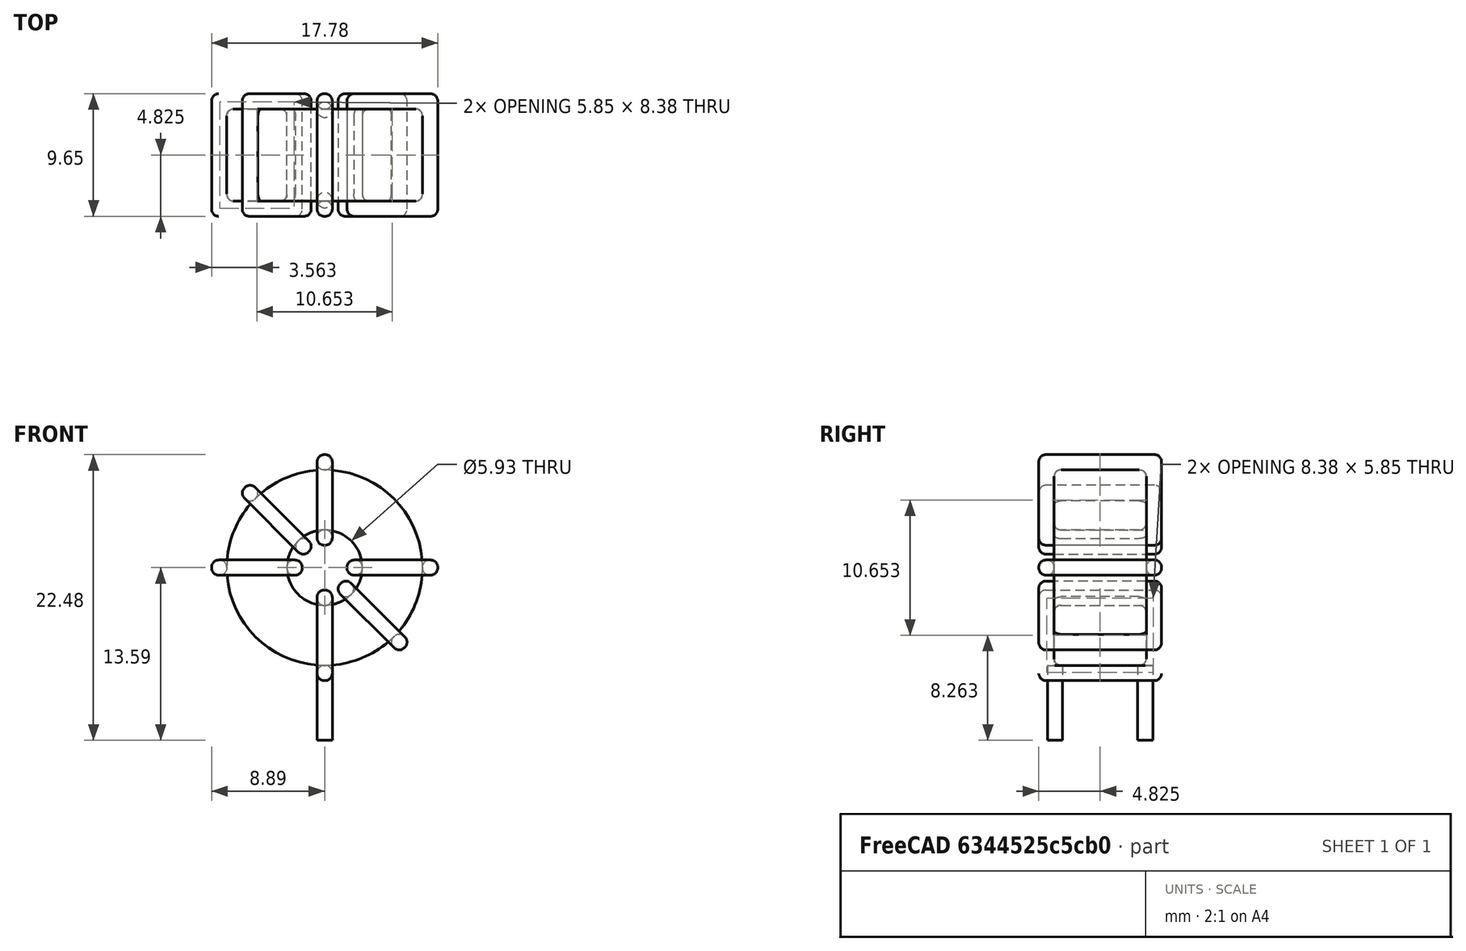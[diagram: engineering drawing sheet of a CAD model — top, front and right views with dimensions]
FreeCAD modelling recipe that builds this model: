
FCSTD DOCUMENT  (FreeCAD 0.16R6703 (Git))
Label: L_Toroid_Vertical_L17.8mm_W9.7mm_P7.11mm_Pulse_B
License: All rights reserved
LicenseURL: http://en.wikipedia.org/wiki/All_rights_reserved
objects: Sketcher::SketchObject×6, PartDesign::Pad×6, PartDesign::Fillet×5, Spreadsheet::Sheet×1
note: 23 computed .brp shape members not serialized (recipe doc carries the construction recipe); baked Part::Feature solids carry a one-line shape summary decoded from their .brp

FEATURE [Spreadsheet::Sheet] Spreadsheet  label="dimensions"
  cells = A1=Wx; B1(Wx)=17.78; C1(WW)=5.926666666666667; D1=17.78; A2=Wy; B2(Wy)=9.65; D2=9.65; A3=RM; B3(RMx)=7.11; C3(RMy)=0; A4=d_wire; B4(d_wire)=1.2; A5=H; B5(H)=17.78; A6=offsetx; B6(offsetx)=8.890000000000001
FEATURE [Sketcher::SketchObject] Sketch
  Placement = pos=(0,-3.555,0) rot=(1,0,0;1.5708rad)
  expr: Placement.Base.y = -Spreadsheet.RMx / 2
  expr: Constraints[0] = Spreadsheet.Wx / 2 - Spreadsheet.d_wire
  expr: Constraints[4] = Spreadsheet.WW / 2
  expr: Constraints[2] = Spreadsheet.Wx / 2 + Spreadsheet.d_wire + 0.5
  sketch-geometry (2):
    g0: Circle CenterX=0 CenterY=10.59 CenterZ=0 NormalX=0 NormalY=0 NormalZ=1 Radius=7.69
    g1: Circle CenterX=0 CenterY=10.59 CenterZ=0 NormalX=0 NormalY=0 NormalZ=1 Radius=2.96333
  constraints (5):
    c: Radius(g0) = 7.69
    c: DistanceX(g-1,g0) = 0
    c: DistanceY(g-1,g0) = 10.59
    c: Coincident(g1,g0)
    c: Radius(g1) = 2.96333
FEATURE [PartDesign::Pad] Pad
  Length = 7.25
  Length2 = 100
  Midplane = true
  Placement = pos=(0,-3.555,0) rot=(1,0,0;1.5708rad)
  Sketch = -> Sketch
  Type = 0
  expr: Length = Spreadsheet.Wy - 2 * Spreadsheet.d_wire
FEATURE [Sketcher::SketchObject] Sketch001
  Placement = pos=(0,0,1.7) rot=(0,0,1;0rad)
  expr: Placement.Base.z = 0.5 + Spreadsheet.d_wire
  expr: Constraints[4] = Spreadsheet.RMy
  expr: Constraints[2] = -Spreadsheet.RMx
  expr: Constraints[1] = Spreadsheet.d_wire / 2
  sketch-geometry (2):
    g0: Circle CenterX=0 CenterY=0 CenterZ=0 NormalX=0 NormalY=0 NormalZ=1 Radius=0.6
    g1: Circle CenterX=0 CenterY=-7.11 CenterZ=0 NormalX=0 NormalY=0 NormalZ=1 Radius=0.6
  constraints (5):
    c: Equal(g0,g1)
    c: Radius(g0) = 0.6
    c: DistanceY(g-1,g1) = -7.11
    c: Coincident(g0,g-1)
    c: DistanceX(g-1,g1) = 0
FEATURE [PartDesign::Pad] Pad001
  Length = 1.2
  Length2 = 4.7
  Placement = pos=(0,0,1.7) rot=(0,0,1;0rad)
  Reversed = true
  Sketch = -> Sketch001
  Type = 4
  expr: Length2 = 3.5 + Spreadsheet.d_wire
  expr: Length = Spreadsheet.d_wire
FEATURE [PartDesign::Fillet] Fillet
  Base = -> Pad [Edge6,Edge3,Edge2]
  Placement = pos=(0,-3.555,0) rot=(1,0,0;1.5708rad)
  Radius = 0.5
FEATURE [Sketcher::SketchObject] Sketch003
  Placement = pos=(0,1.27,10.59) rot=(1,0,0;3.14159rad)
  expr: Constraints[18] = Spreadsheet.d_wire
  expr: Constraints[16] = Spreadsheet.d_wire
  expr: Constraints[19] = Spreadsheet.d_wire
  expr: Constraints[17] = Spreadsheet.d_wire
  expr: Placement.Base.y = -1 * (Spreadsheet.RMx - Spreadsheet.Wy) / 2
  expr: Constraints[21] = (Spreadsheet.Wx - Spreadsheet.WW) / 2 - Spreadsheet.d_wire
  expr: Constraints[22] = Spreadsheet.Wx / 2 - Spreadsheet.d_wire
  expr: Constraints[43] = Spreadsheet.d_wire
  expr: Constraints[48] = Spreadsheet.Wx - Spreadsheet.d_wire * 2
  expr: Constraints[49] = Spreadsheet.Wy
  expr: Placement.Base.z = Spreadsheet.Wx / 2 + Spreadsheet.d_wire + 0.5
  sketch-geometry (16):
    g0: LineSegment StartX=-1.76333 StartY=0 StartZ=0 EndX=-8.89 EndY=0 EndZ=0
    g1: LineSegment StartX=-8.89 StartY=0 StartZ=0 EndX=-8.89 EndY=9.65 EndZ=0
    g2: LineSegment StartX=-8.89 StartY=9.65 StartZ=0 EndX=-1.76333 EndY=9.65 EndZ=0
    g3: LineSegment StartX=-1.76333 StartY=9.65 StartZ=0 EndX=-1.76333 EndY=0 EndZ=0
    g4: LineSegment StartX=-7.69 StartY=8.45 StartZ=0 EndX=-2.96333 EndY=8.45 EndZ=0
    g5: LineSegment StartX=-2.96333 StartY=8.45 StartZ=0 EndX=-2.96333 EndY=1.2 EndZ=0
    g6: LineSegment StartX=-2.96333 StartY=1.2 StartZ=0 EndX=-7.69 EndY=1.2 EndZ=0
    g7: LineSegment StartX=-7.69 StartY=1.2 StartZ=0 EndX=-7.69 EndY=8.45 EndZ=0
    g8: LineSegment StartX=1.76333 StartY=9.65 StartZ=0 EndX=8.89 EndY=9.65 EndZ=0
    g9: LineSegment StartX=8.89 StartY=9.65 StartZ=0 EndX=8.89 EndY=0 EndZ=0
    g10: LineSegment StartX=8.89 StartY=0 StartZ=0 EndX=1.76333 EndY=0 EndZ=0
    g11: LineSegment StartX=1.76333 StartY=0 StartZ=0 EndX=1.76333 EndY=9.65 EndZ=0
    g12: LineSegment StartX=2.96333 StartY=8.45 StartZ=0 EndX=7.69 EndY=8.45 EndZ=0
    g13: LineSegment StartX=7.69 StartY=8.45 StartZ=0 EndX=7.69 EndY=1.2 EndZ=0
    g14: LineSegment StartX=7.69 StartY=1.2 StartZ=0 EndX=2.96333 EndY=1.2 EndZ=0
    g15: LineSegment StartX=2.96333 StartY=1.2 StartZ=0 EndX=2.96333 EndY=8.45 EndZ=0
  constraints (50):
    c: Horizontal(g0)
    c: Coincident(g1,g0)
    c: Vertical(g1)
    c: Coincident(g2,g1)
    c: Horizontal(g2)
    c: Coincident(g3,g2)
    c: Coincident(g3,g0)
    c: Vertical(g3)
    c: Coincident(g4,g5)
    c: Coincident(g5,g6)
    c: Coincident(g6,g7)
    c: Coincident(g7,g4)
    c: Horizontal(g4)
    c: Horizontal(g6)
    c: Vertical(g5)
    c: Vertical(g7)
    c: DistanceX(g1,g4) = 1.2
    c: DistanceY(g4,g1) = 1.2
    c: DistanceX(g5,g0) = 1.2
    c: DistanceY(g0,g5) = 1.2
    c: DistanceY(g-1,g0) = 0
    c: DistanceX(g6,g6) = 4.72667
    c: DistanceX(g6,g-1) = 7.69
    c: Coincident(g8,g9)
    c: Coincident(g9,g10)
    c: Coincident(g10,g11)
    c: Coincident(g11,g8)
    c: Horizontal(g8)
    c: Horizontal(g10)
    c: Vertical(g9)
    c: Vertical(g11)
    c: Coincident(g12,g13)
    c: Coincident(g13,g14)
    c: Coincident(g14,g15)
    c: Coincident(g15,g12)
    c: Horizontal(g12)
    c: Horizontal(g14)
    c: Vertical(g13)
    c: Vertical(g15)
    c: DistanceY(g8,g2) = 0
    c: DistanceY(g10,g0) = 0
    c: DistanceY(g14,g5) = 0
    c: DistanceY(g12,g4) = 0
    c: DistanceX(g8,g12) = 1.2
    c: Equal(g8,g2)
    c: Equal(g12,g4)
    c: Equal(g9,g1)
    c: Equal(g13,g7)
    c: DistanceX(g4,g12) = 15.38
    c: DistanceY(g0,g1) = 9.65
FEATURE [PartDesign::Pad] Pad002
  Length = 1.2
  Length2 = 100
  Midplane = true
  Placement = pos=(0,1.27,10.59) rot=(1,0,0;3.14159rad)
  Sketch = -> Sketch003
  Type = 0
  expr: Length = Spreadsheet.d_wire
FEATURE [PartDesign::Fillet] Fillet001
  Base = -> Pad002 [Edge38,Edge41,Edge42,Edge43,Edge29,Edge32,Edge33,Edge34,Edge25,Edge35,Edge36,Edge13,Edge14,Edge15,Edge16,Edge17,Edge18,Edge19,Edge1,Edge2,Edge3,Edge4,Edge5,Edge6,Edge7,Edge37,Edge39,Edge40,Edge20,Edge23,Edge24,Edge21,Edge22,Edge8,Edge9,Edge10,Edge11,Edge12,Edge26,Edge27,+8 more]
  Placement = pos=(0,1.27,10.59) rot=(1,0,0;3.14159rad)
  Radius = 0.564
  expr: Radius = Spreadsheet.d_wire * 0.47
FEATURE [Sketcher::SketchObject] Sketch004
  Placement = pos=(0,1.27,10.59) rot=(0.92388,0,0.382683;3.14159rad)
  expr: Constraints[18] = Spreadsheet.d_wire
  expr: Constraints[16] = Spreadsheet.d_wire
  expr: Constraints[19] = Spreadsheet.d_wire
  expr: Constraints[17] = Spreadsheet.d_wire
  expr: Placement.Base.y = -1 * (Spreadsheet.RMx - Spreadsheet.Wy) / 2
  expr: Constraints[21] = (Spreadsheet.Wx - Spreadsheet.WW) / 2 - Spreadsheet.d_wire
  expr: Constraints[22] = Spreadsheet.Wx / 2 - Spreadsheet.d_wire
  expr: Constraints[43] = Spreadsheet.d_wire
  expr: Constraints[48] = Spreadsheet.Wx - 2 * Spreadsheet.d_wire
  expr: Constraints[49] = Spreadsheet.Wy
  expr: Placement.Base.z = Spreadsheet.Wx / 2 + Spreadsheet.d_wire + 0.5
  sketch-geometry (16):
    g0: LineSegment StartX=-1.76333 StartY=0 StartZ=0 EndX=-8.89 EndY=0 EndZ=0
    g1: LineSegment StartX=-8.89 StartY=0 StartZ=0 EndX=-8.89 EndY=9.65 EndZ=0
    g2: LineSegment StartX=-8.89 StartY=9.65 StartZ=0 EndX=-1.76333 EndY=9.65 EndZ=0
    g3: LineSegment StartX=-1.76333 StartY=9.65 StartZ=0 EndX=-1.76333 EndY=0 EndZ=0
    g4: LineSegment StartX=-7.69 StartY=8.45 StartZ=0 EndX=-2.96333 EndY=8.45 EndZ=0
    g5: LineSegment StartX=-2.96333 StartY=8.45 StartZ=0 EndX=-2.96333 EndY=1.2 EndZ=0
    g6: LineSegment StartX=-2.96333 StartY=1.2 StartZ=0 EndX=-7.69 EndY=1.2 EndZ=0
    g7: LineSegment StartX=-7.69 StartY=1.2 StartZ=0 EndX=-7.69 EndY=8.45 EndZ=0
    g8: LineSegment StartX=1.76333 StartY=9.65 StartZ=0 EndX=8.89 EndY=9.65 EndZ=0
    g9: LineSegment StartX=8.89 StartY=9.65 StartZ=0 EndX=8.89 EndY=0 EndZ=0
    g10: LineSegment StartX=8.89 StartY=0 StartZ=0 EndX=1.76333 EndY=0 EndZ=0
    g11: LineSegment StartX=1.76333 StartY=0 StartZ=0 EndX=1.76333 EndY=9.65 EndZ=0
    g12: LineSegment StartX=2.96333 StartY=8.45 StartZ=0 EndX=7.69 EndY=8.45 EndZ=0
    g13: LineSegment StartX=7.69 StartY=8.45 StartZ=0 EndX=7.69 EndY=1.2 EndZ=0
    g14: LineSegment StartX=7.69 StartY=1.2 StartZ=0 EndX=2.96333 EndY=1.2 EndZ=0
    g15: LineSegment StartX=2.96333 StartY=1.2 StartZ=0 EndX=2.96333 EndY=8.45 EndZ=0
  constraints (50):
    c: Horizontal(g0)
    c: Coincident(g1,g0)
    c: Vertical(g1)
    c: Coincident(g2,g1)
    c: Horizontal(g2)
    c: Coincident(g3,g2)
    c: Coincident(g3,g0)
    c: Vertical(g3)
    c: Coincident(g4,g5)
    c: Coincident(g5,g6)
    c: Coincident(g6,g7)
    c: Coincident(g7,g4)
    c: Horizontal(g4)
    c: Horizontal(g6)
    c: Vertical(g5)
    c: Vertical(g7)
    c: DistanceX(g1,g4) = 1.2
    c: DistanceY(g4,g1) = 1.2
    c: DistanceX(g5,g0) = 1.2
    c: DistanceY(g0,g5) = 1.2
    c: DistanceY(g-1,g0) = 0
    c: DistanceX(g6,g6) = 4.72667
    c: DistanceX(g6,g-1) = 7.69
    c: Coincident(g8,g9)
    c: Coincident(g9,g10)
    c: Coincident(g10,g11)
    c: Coincident(g11,g8)
    c: Horizontal(g8)
    c: Horizontal(g10)
    c: Vertical(g9)
    c: Vertical(g11)
    c: Coincident(g12,g13)
    c: Coincident(g13,g14)
    c: Coincident(g14,g15)
    c: Coincident(g15,g12)
    c: Horizontal(g12)
    c: Horizontal(g14)
    c: Vertical(g13)
    c: Vertical(g15)
    c: DistanceY(g8,g2) = 0
    c: DistanceY(g10,g0) = 0
    c: DistanceY(g14,g5) = 0
    c: DistanceY(g12,g4) = 0
    c: DistanceX(g8,g12) = 1.2
    c: Equal(g8,g2)
    c: Equal(g12,g4)
    c: Equal(g9,g1)
    c: Equal(g13,g7)
    c: DistanceX(g4,g12) = 15.38
    c: DistanceY(g0,g1) = 9.65
FEATURE [PartDesign::Pad] Pad003
  Length = 1.2
  Length2 = 100
  Midplane = true
  Placement = pos=(0,1.27,10.59) rot=(0.92388,0,0.382683;3.14159rad)
  Sketch = -> Sketch004
  Type = 0
  expr: Length = Spreadsheet.d_wire
FEATURE [PartDesign::Fillet] Fillet002
  Base = -> Pad003 [Edge38,Edge41,Edge42,Edge43,Edge29,Edge32,Edge33,Edge34,Edge25,Edge35,Edge36,Edge13,Edge14,Edge15,Edge16,Edge17,Edge18,Edge19,Edge1,Edge2,Edge3,Edge4,Edge5,Edge6,Edge7,Edge37,Edge39,Edge40,Edge20,Edge23,Edge24,Edge21,Edge22,Edge8,Edge9,Edge10,Edge11,Edge12,Edge26,Edge27,+8 more]
  Placement = pos=(0,1.27,10.59) rot=(0.92388,0,0.382683;3.14159rad)
  Radius = 0.564
  expr: Radius = Spreadsheet.d_wire * 0.47
FEATURE [Sketcher::SketchObject] Sketch005
  Placement = pos=(0,1.27,10.59) rot=(0.92388,0,-0.382683;3.14159rad)
  expr: Constraints[18] = Spreadsheet.d_wire
  expr: Constraints[16] = Spreadsheet.d_wire
  expr: Constraints[19] = Spreadsheet.d_wire
  expr: Constraints[17] = Spreadsheet.d_wire
  expr: Placement.Base.y = -1 * (Spreadsheet.RMx - Spreadsheet.Wy) / 2
  expr: Constraints[21] = (Spreadsheet.Wx - Spreadsheet.WW) / 2 - Spreadsheet.d_wire
  expr: Constraints[22] = Spreadsheet.Wx / 2 - Spreadsheet.d_wire
  expr: Constraints[43] = Spreadsheet.d_wire
  expr: Constraints[48] = Spreadsheet.Wx - 2 * Spreadsheet.d_wire
  expr: Constraints[49] = Spreadsheet.Wy
  expr: Placement.Base.z = Spreadsheet.Wx / 2 + Spreadsheet.d_wire + 0.5
  sketch-geometry (16):
    g0: LineSegment StartX=-1.76333 StartY=0 StartZ=0 EndX=-8.89 EndY=0 EndZ=0
    g1: LineSegment StartX=-8.89 StartY=0 StartZ=0 EndX=-8.89 EndY=9.65 EndZ=0
    g2: LineSegment StartX=-8.89 StartY=9.65 StartZ=0 EndX=-1.76333 EndY=9.65 EndZ=0
    g3: LineSegment StartX=-1.76333 StartY=9.65 StartZ=0 EndX=-1.76333 EndY=0 EndZ=0
    g4: LineSegment StartX=-7.69 StartY=8.45 StartZ=0 EndX=-2.96333 EndY=8.45 EndZ=0
    g5: LineSegment StartX=-2.96333 StartY=8.45 StartZ=0 EndX=-2.96333 EndY=1.2 EndZ=0
    g6: LineSegment StartX=-2.96333 StartY=1.2 StartZ=0 EndX=-7.69 EndY=1.2 EndZ=0
    g7: LineSegment StartX=-7.69 StartY=1.2 StartZ=0 EndX=-7.69 EndY=8.45 EndZ=0
    g8: LineSegment StartX=1.76333 StartY=9.65 StartZ=0 EndX=8.89 EndY=9.65 EndZ=0
    g9: LineSegment StartX=8.89 StartY=9.65 StartZ=0 EndX=8.89 EndY=0 EndZ=0
    g10: LineSegment StartX=8.89 StartY=0 StartZ=0 EndX=1.76333 EndY=0 EndZ=0
    g11: LineSegment StartX=1.76333 StartY=0 StartZ=0 EndX=1.76333 EndY=9.65 EndZ=0
    g12: LineSegment StartX=2.96333 StartY=8.45 StartZ=0 EndX=7.69 EndY=8.45 EndZ=0
    g13: LineSegment StartX=7.69 StartY=8.45 StartZ=0 EndX=7.69 EndY=1.2 EndZ=0
    g14: LineSegment StartX=7.69 StartY=1.2 StartZ=0 EndX=2.96333 EndY=1.2 EndZ=0
    g15: LineSegment StartX=2.96333 StartY=1.2 StartZ=0 EndX=2.96333 EndY=8.45 EndZ=0
  constraints (50):
    c: Horizontal(g0)
    c: Coincident(g1,g0)
    c: Vertical(g1)
    c: Coincident(g2,g1)
    c: Horizontal(g2)
    c: Coincident(g3,g2)
    c: Coincident(g3,g0)
    c: Vertical(g3)
    c: Coincident(g4,g5)
    c: Coincident(g5,g6)
    c: Coincident(g6,g7)
    c: Coincident(g7,g4)
    c: Horizontal(g4)
    c: Horizontal(g6)
    c: Vertical(g5)
    c: Vertical(g7)
    c: DistanceX(g1,g4) = 1.2
    c: DistanceY(g4,g1) = 1.2
    c: DistanceX(g5,g0) = 1.2
    c: DistanceY(g0,g5) = 1.2
    c: DistanceY(g-1,g0) = 0
    c: DistanceX(g6,g6) = 4.72667
    c: DistanceX(g6,g-1) = 7.69
    c: Coincident(g8,g9)
    c: Coincident(g9,g10)
    c: Coincident(g10,g11)
    c: Coincident(g11,g8)
    c: Horizontal(g8)
    c: Horizontal(g10)
    c: Vertical(g9)
    c: Vertical(g11)
    c: Coincident(g12,g13)
    c: Coincident(g13,g14)
    c: Coincident(g14,g15)
    c: Coincident(g15,g12)
    c: Horizontal(g12)
    c: Horizontal(g14)
    c: Vertical(g13)
    c: Vertical(g15)
    c: DistanceY(g8,g2) = 0
    c: DistanceY(g10,g0) = 0
    c: DistanceY(g14,g5) = 0
    c: DistanceY(g12,g4) = 0
    c: DistanceX(g8,g12) = 1.2
    c: Equal(g8,g2)
    c: Equal(g12,g4)
    c: Equal(g9,g1)
    c: Equal(g13,g7)
    c: DistanceX(g4,g12) = 15.38
    c: DistanceY(g0,g1) = 9.65
FEATURE [PartDesign::Pad] Pad004
  Length = 1.2
  Length2 = 100
  Midplane = true
  Placement = pos=(0,1.27,10.59) rot=(0.92388,0,-0.382683;3.14159rad)
  Sketch = -> Sketch005
  Type = 0
  expr: Length = Spreadsheet.d_wire
FEATURE [PartDesign::Fillet] Fillet003
  Base = -> Pad004 [Edge38,Edge41,Edge42,Edge43,Edge29,Edge32,Edge33,Edge34,Edge25,Edge35,Edge36,Edge13,Edge14,Edge15,Edge16,Edge17,Edge18,Edge19,Edge1,Edge2,Edge3,Edge4,Edge5,Edge6,Edge7,Edge37,Edge39,Edge40,Edge20,Edge23,Edge24,Edge21,Edge22,Edge8,Edge9,Edge10,Edge11,Edge12,Edge26,Edge27,+8 more]
  Placement = pos=(0,1.27,10.59) rot=(0.92388,0,-0.382683;3.14159rad)
  Radius = 0.564
  expr: Radius = Spreadsheet.d_wire * 0.47
FEATURE [Sketcher::SketchObject] Sketch006
  Placement = pos=(0,1.27,10.59) rot=(0.707107,0,0.707107;3.14159rad)
  expr: Constraints[18] = Spreadsheet.d_wire
  expr: Constraints[16] = Spreadsheet.d_wire
  expr: Constraints[19] = Spreadsheet.d_wire
  expr: Constraints[17] = Spreadsheet.d_wire
  expr: Placement.Base.y = -1 * (Spreadsheet.RMx - Spreadsheet.Wy) / 2
  expr: Constraints[21] = (Spreadsheet.Wx - Spreadsheet.WW) / 2 - Spreadsheet.d_wire
  expr: Constraints[22] = Spreadsheet.Wx / 2 - Spreadsheet.d_wire
  expr: Constraints[43] = Spreadsheet.d_wire
  expr: Constraints[48] = Spreadsheet.Wx - Spreadsheet.d_wire * 2
  expr: Constraints[49] = Spreadsheet.Wy
  expr: Placement.Base.z = Spreadsheet.Wx / 2 + Spreadsheet.d_wire + 0.5
  sketch-geometry (16):
    g0: LineSegment StartX=-1.76333 StartY=0 StartZ=0 EndX=-8.89 EndY=0 EndZ=0
    g1: LineSegment StartX=-8.89 StartY=0 StartZ=0 EndX=-8.89 EndY=9.65 EndZ=0
    g2: LineSegment StartX=-8.89 StartY=9.65 StartZ=0 EndX=-1.76333 EndY=9.65 EndZ=0
    g3: LineSegment StartX=-1.76333 StartY=9.65 StartZ=0 EndX=-1.76333 EndY=0 EndZ=0
    g4: LineSegment StartX=-7.69 StartY=8.45 StartZ=0 EndX=-2.96333 EndY=8.45 EndZ=0
    g5: LineSegment StartX=-2.96333 StartY=8.45 StartZ=0 EndX=-2.96333 EndY=1.2 EndZ=0
    g6: LineSegment StartX=-2.96333 StartY=1.2 StartZ=0 EndX=-7.69 EndY=1.2 EndZ=0
    g7: LineSegment StartX=-7.69 StartY=1.2 StartZ=0 EndX=-7.69 EndY=8.45 EndZ=0
    g8: LineSegment StartX=1.76333 StartY=9.65 StartZ=0 EndX=8.89 EndY=9.65 EndZ=0
    g9: LineSegment StartX=8.89 StartY=9.65 StartZ=0 EndX=8.89 EndY=0 EndZ=0
    g10: LineSegment StartX=8.89 StartY=0 StartZ=0 EndX=1.76333 EndY=0 EndZ=0
    g11: LineSegment StartX=1.76333 StartY=0 StartZ=0 EndX=1.76333 EndY=9.65 EndZ=0
    g12: LineSegment StartX=2.96333 StartY=8.45 StartZ=0 EndX=7.69 EndY=8.45 EndZ=0
    g13: LineSegment StartX=7.69 StartY=8.45 StartZ=0 EndX=7.69 EndY=1.2 EndZ=0
    g14: LineSegment StartX=7.69 StartY=1.2 StartZ=0 EndX=2.96333 EndY=1.2 EndZ=0
    g15: LineSegment StartX=2.96333 StartY=1.2 StartZ=0 EndX=2.96333 EndY=8.45 EndZ=0
  constraints (50):
    c: Horizontal(g0)
    c: Coincident(g1,g0)
    c: Vertical(g1)
    c: Coincident(g2,g1)
    c: Horizontal(g2)
    c: Coincident(g3,g2)
    c: Coincident(g3,g0)
    c: Vertical(g3)
    c: Coincident(g4,g5)
    c: Coincident(g5,g6)
    c: Coincident(g6,g7)
    c: Coincident(g7,g4)
    c: Horizontal(g4)
    c: Horizontal(g6)
    c: Vertical(g5)
    c: Vertical(g7)
    c: DistanceX(g1,g4) = 1.2
    c: DistanceY(g4,g1) = 1.2
    c: DistanceX(g5,g0) = 1.2
    c: DistanceY(g0,g5) = 1.2
    c: DistanceY(g-1,g0) = 0
    c: DistanceX(g6,g6) = 4.72667
    c: DistanceX(g6,g-1) = 7.69
    c: Coincident(g8,g9)
    c: Coincident(g9,g10)
    c: Coincident(g10,g11)
    c: Coincident(g11,g8)
    c: Horizontal(g8)
    c: Horizontal(g10)
    c: Vertical(g9)
    c: Vertical(g11)
    c: Coincident(g12,g13)
    c: Coincident(g13,g14)
    c: Coincident(g14,g15)
    c: Coincident(g15,g12)
    c: Horizontal(g12)
    c: Horizontal(g14)
    c: Vertical(g13)
    c: Vertical(g15)
    c: DistanceY(g8,g2) = 0
    c: DistanceY(g10,g0) = 0
    c: DistanceY(g14,g5) = 0
    c: DistanceY(g12,g4) = 0
    c: DistanceX(g8,g12) = 1.2
    c: Equal(g8,g2)
    c: Equal(g12,g4)
    c: Equal(g9,g1)
    c: Equal(g13,g7)
    c: DistanceX(g4,g12) = 15.38
    c: DistanceY(g0,g1) = 9.65
FEATURE [PartDesign::Pad] Pad005
  Length = 1.2
  Length2 = 100
  Midplane = true
  Placement = pos=(0,1.27,10.59) rot=(0.707107,0,0.707107;3.14159rad)
  Sketch = -> Sketch006
  Type = 0
  expr: Length = Spreadsheet.d_wire
FEATURE [PartDesign::Fillet] Fillet004
  Base = -> Pad005 [Edge38,Edge41,Edge42,Edge43,Edge29,Edge32,Edge33,Edge34,Edge25,Edge35,Edge36,Edge13,Edge14,Edge15,Edge16,Edge17,Edge18,Edge19,Edge1,Edge2,Edge3,Edge4,Edge5,Edge6,Edge7,Edge37,Edge39,Edge40,Edge20,Edge23,Edge24,Edge21,Edge22,Edge8,Edge9,Edge10,Edge11,Edge12,Edge26,Edge27,+8 more]
  Placement = pos=(0,1.27,10.59) rot=(0.707107,0,0.707107;3.14159rad)
  Radius = 0.564
  expr: Radius = Spreadsheet.d_wire * 0.47
